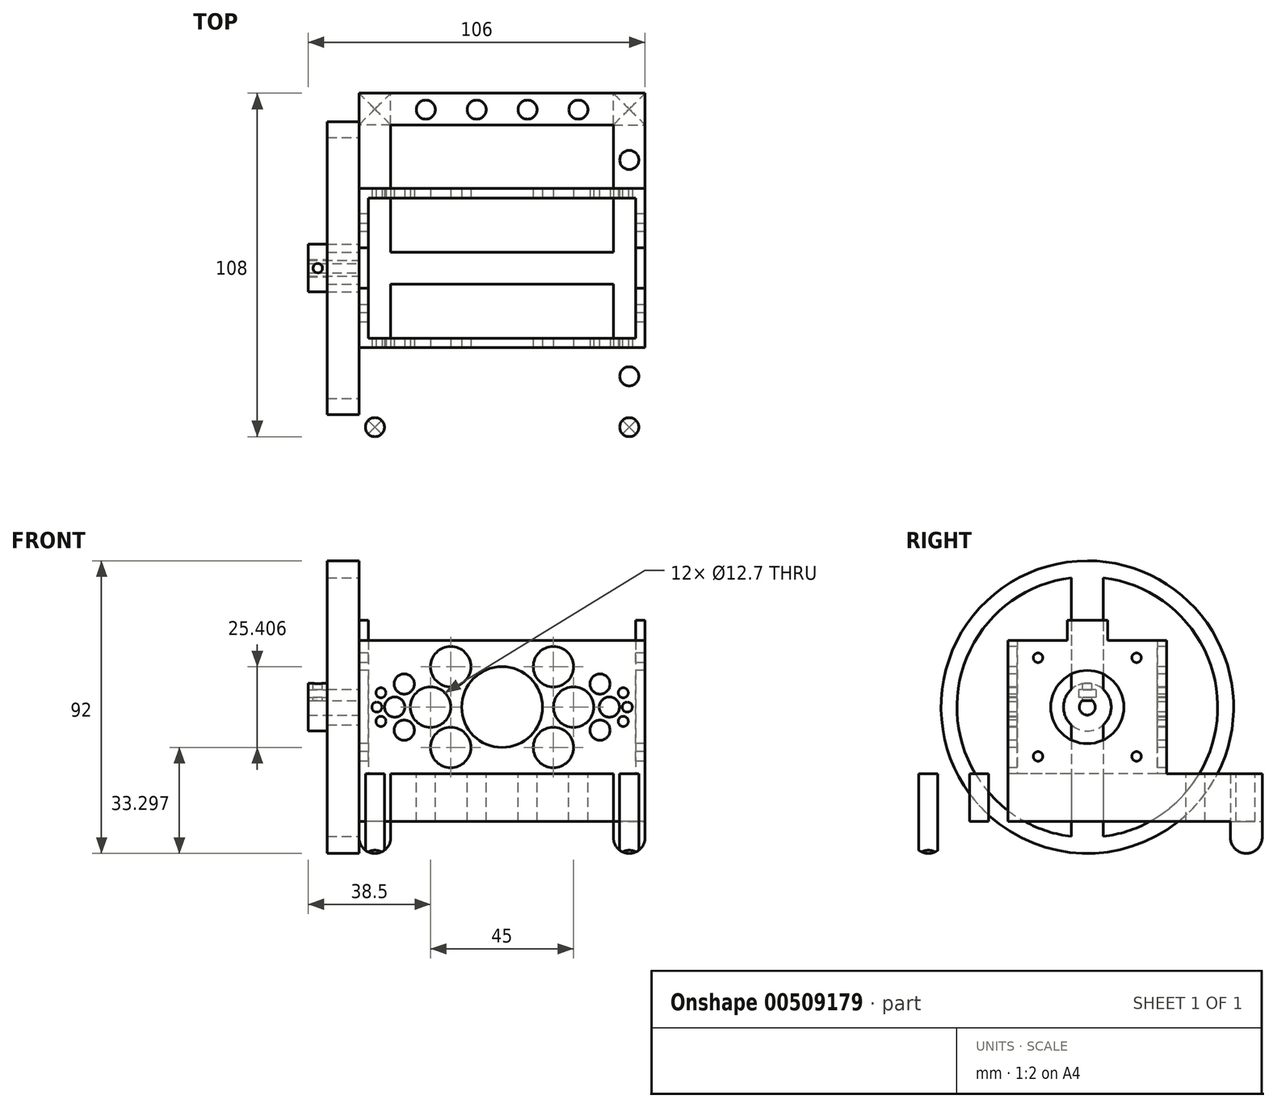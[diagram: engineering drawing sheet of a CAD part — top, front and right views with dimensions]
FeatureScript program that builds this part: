
annotation { "Feature Type Name" : "Feature", "Feature Type Description" : "" }
export const myFeature = defineFeature(function(context is Context, id is Id, definition is map)
    precondition{}
    {
        {
            var Q0;
            Q0=qCreatedBy(makeId("Top.planeOp"),FACE);
            var sketch = newSketch(context, id + "F0", { "sketchPlane" : qUnion([Q0])});
            skLineSegment(sketch, "E0.bottom", {"start": v(-45, 55) * mm, "end": v(45, 55) * mm});
            skLineSegment(sketch, "E0.top", {"start": v(-45, -55) * mm, "end": v(45, -55) * mm});
            skLineSegment(sketch, "E0.left", {"start": v(-45, 55) * mm, "end": v(-45, -55) * mm});
            skLineSegment(sketch, "E0.right", {"start": v(45, 55) * mm, "end": v(45, -55) * mm});
            skPoint(sketch, "E1", {"position": v(0, 55) * mm});
            skPoint(sketch, "E2", {"position": v(45, 0) * mm});
            skLineSegment(sketch, "E3.bottom", {"start": v(-35, 45) * mm, "end": v(35, 45) * mm});
            skLineSegment(sketch, "E3.top", {"start": v(-35, -45) * mm, "end": v(35, -45) * mm});
            skLineSegment(sketch, "E3.left", {"start": v(-35, 45) * mm, "end": v(-35, 5) * mm});
            skLineSegment(sketch, "E3.right", {"start": v(35, 45) * mm, "end": v(35, 5) * mm});
            skPoint(sketch, "E4", {"position": v(0, 45) * mm});
            skPoint(sketch, "E5", {"position": v(35, 0) * mm});
            skLineSegment(sketch, "E6", {"start": v(-35, 5) * mm, "end": v(35, 5) * mm});
            skLineSegment(sketch, "E7", {"start": v(-35, -5) * mm, "end": v(35, -5) * mm});
            skPoint(sketch, "E8", {"position": v(-35, 0) * mm});
            skLineSegment(sketch, "E9.trimOffspring", {"start": v(-35, -5) * mm, "end": v(-35, -45) * mm});
            skLineSegment(sketch, "E10.trimOffspring", {"start": v(35, -5) * mm, "end": v(35, -45) * mm});
            skSolve(sketch);
        }
        {
            var Q0;
            Q0 = qSketchRegion(id + "F0", true);
            extrude(context, id + "F1", {"entities" : qUnion([Q0]), "depth" : 15 * mm});
        }
        {
            var Q0;
            Q0=makeQuery(id+"F1.opExtrude","CAP_FACE",FACE,{"disambiguationData":[OSD([sQuery(id+"F0.wireOp",EDGE,"E0.bottom"),sQuery(id+"F0.wireOp",EDGE,"E0.top"),sQuery(id+"F0.wireOp",EDGE,"E0.left"),sQuery(id+"F0.wireOp",EDGE,"E0.right"),sQuery(id+"F0.wireOp",EDGE,"E3.bottom"),sQuery(id+"F0.wireOp",EDGE,"E3.top"),sQuery(id+"F0.wireOp",EDGE,"E3.left"),sQuery(id+"F0.wireOp",EDGE,"E3.right"),sQuery(id+"F0.wireOp",EDGE,"E6"),sQuery(id+"F0.wireOp",EDGE,"E7"),sQuery(id+"F0.wireOp",EDGE,"E9.trimOffspring"),sQuery(id+"F0.wireOp",EDGE,"E10.trimOffspring")])],"isStart":false});
            var sketch = newSketch(context, id + "F2", { "sketchPlane" : qUnion([Q0])});
            skLineSegment(sketch, "E11.bottom", {"start": v(45, 25) * mm, "end": v(42, 25) * mm});
            skLineSegment(sketch, "E11.top", {"start": v(45, -25) * mm, "end": v(42, -25) * mm});
            skLineSegment(sketch, "E11.left", {"start": v(45, 25) * mm, "end": v(45, -25) * mm});
            skLineSegment(sketch, "E11.right", {"start": v(42, 25) * mm, "end": v(42, -25) * mm});
            skPoint(sketch, "E12", {"position": v(45, 0) * mm});
            skLineSegment(sketch, "E13.bottom", {"start": v(45, 25) * mm, "end": v(35, 25) * mm});
            skLineSegment(sketch, "E13.top", {"start": v(45, 22) * mm, "end": v(35, 22) * mm});
            skLineSegment(sketch, "E13.left", {"start": v(45, 25) * mm, "end": v(45, 22) * mm});
            skLineSegment(sketch, "E13.right", {"start": v(35, 25) * mm, "end": v(35, 22) * mm});
            skLineSegment(sketch, "E14.MirrorCS", {"start": v(35, -25) * mm, "end": v(35, -22) * mm});
            skLineSegment(sketch, "E15.MirrorCS", {"start": v(45, -22) * mm, "end": v(35, -22) * mm});
            skLineSegment(sketch, "E16.MirrorCS", {"start": v(45, -25) * mm, "end": v(35, -25) * mm});
            skLineSegment(sketch, "E17.MirrorCS", {"start": v(-45, 25) * mm, "end": v(-45, 22) * mm});
            skLineSegment(sketch, "E18.MirrorCS", {"start": v(-35, 25) * mm, "end": v(-35, 22) * mm});
            skLineSegment(sketch, "E19.MirrorCS", {"start": v(-45, 25) * mm, "end": v(-42, 25) * mm});
            skLineSegment(sketch, "E20.MirrorCS", {"start": v(-45, -25) * mm, "end": v(-42, -25) * mm});
            skLineSegment(sketch, "E21.MirrorCS", {"start": v(-35, -25) * mm, "end": v(-35, -22) * mm});
            skLineSegment(sketch, "E22.MirrorCS", {"start": v(-42, 25) * mm, "end": v(-42, -25) * mm});
            skLineSegment(sketch, "E23.MirrorCS", {"start": v(-45, 25) * mm, "end": v(-35, 25) * mm});
            skLineSegment(sketch, "E24.MirrorCS", {"start": v(-45, -22) * mm, "end": v(-35, -22) * mm});
            skPoint(sketch, "E25.MirrorP", {"position": v(-45, 0) * mm});
            skLineSegment(sketch, "E26.MirrorCS", {"start": v(-45, -25) * mm, "end": v(-35, -25) * mm});
            skLineSegment(sketch, "E27.MirrorCS", {"start": v(-45, 25) * mm, "end": v(-45, -25) * mm});
            skLineSegment(sketch, "E28.MirrorCS", {"start": v(-45, 22) * mm, "end": v(-35, 22) * mm});
            skLineSegment(sketch, "E29", {"start": v(35, 25) * mm, "end": v(-35, 25) * mm});
            skLineSegment(sketch, "E30", {"start": v(-35, 22) * mm, "end": v(35, 22) * mm});
            skLineSegment(sketch, "E31", {"start": v(35, -22) * mm, "end": v(-35, -22) * mm});
            skLineSegment(sketch, "E32", {"start": v(-35, -25) * mm, "end": v(35, -25) * mm});
            skSolve(sketch);
        }
        {
            var Q0;
            Q0 = qSketchRegion(id + "F2", true);
            extrude(context, id + "F3", {"entities" : qUnion([Q0]), "operationType" : NewBodyOperationType.ADD, "depth" : 42 * mm});
        }
        {
            var Q0;
            Q0=makeQuery(id+"F1.opExtrude","CAP_FACE",FACE,{"disambiguationData":[OSD([sQuery(id+"F0.wireOp",EDGE,"E0.bottom"),sQuery(id+"F0.wireOp",EDGE,"E0.top"),sQuery(id+"F0.wireOp",EDGE,"E0.left"),sQuery(id+"F0.wireOp",EDGE,"E0.right"),sQuery(id+"F0.wireOp",EDGE,"E3.bottom"),sQuery(id+"F0.wireOp",EDGE,"E3.top"),sQuery(id+"F0.wireOp",EDGE,"E3.left"),sQuery(id+"F0.wireOp",EDGE,"E3.right"),sQuery(id+"F0.wireOp",EDGE,"E6"),sQuery(id+"F0.wireOp",EDGE,"E7"),sQuery(id+"F0.wireOp",EDGE,"E9.trimOffspring"),sQuery(id+"F0.wireOp",EDGE,"E10.trimOffspring")])],"isStart":true});
            var sketch = newSketch(context, id + "F4", { "sketchPlane" : qUnion([Q0])});
            skLineSegment(sketch, "E33.bottom", {"start": v(-35, -45) * mm, "end": v(-45, -45) * mm});
            skLineSegment(sketch, "E33.top", {"start": v(-35, -55) * mm, "end": v(-45, -55) * mm});
            skLineSegment(sketch, "E33.left", {"start": v(-35, -45) * mm, "end": v(-35, -55) * mm});
            skLineSegment(sketch, "E33.right", {"start": v(-45, -45) * mm, "end": v(-45, -55) * mm});
            skLineSegment(sketch, "E34.MirrorCS", {"start": v(-45, 45) * mm, "end": v(-45, 55) * mm});
            skLineSegment(sketch, "E35.MirrorCS", {"start": v(-35, 45) * mm, "end": v(-35, 55) * mm});
            skLineSegment(sketch, "E36.MirrorCS", {"start": v(-35, 55) * mm, "end": v(-45, 55) * mm});
            skLineSegment(sketch, "E37.MirrorCS", {"start": v(-35, 45) * mm, "end": v(-45, 45) * mm});
            skLineSegment(sketch, "E38.MirrorCS", {"start": v(35, 45) * mm, "end": v(45, 45) * mm});
            skLineSegment(sketch, "E39.MirrorCS", {"start": v(35, 55) * mm, "end": v(45, 55) * mm});
            skLineSegment(sketch, "E40.MirrorCS", {"start": v(35, 45) * mm, "end": v(35, 55) * mm});
            skLineSegment(sketch, "E41.MirrorCS", {"start": v(45, 45) * mm, "end": v(45, 55) * mm});
            skLineSegment(sketch, "E42.MirrorCS", {"start": v(45, -45) * mm, "end": v(45, -55) * mm});
            skLineSegment(sketch, "E43.MirrorCS", {"start": v(35, -45) * mm, "end": v(45, -45) * mm});
            skLineSegment(sketch, "E44.MirrorCS", {"start": v(35, -45) * mm, "end": v(35, -55) * mm});
            skLineSegment(sketch, "E45.MirrorCS", {"start": v(35, -55) * mm, "end": v(45, -55) * mm});
            skSolve(sketch);
        }
        {
            var Q0;
            Q0 = qSketchRegion(id + "F4", true);
            extrude(context, id + "F5", {"entities" : qUnion([Q0]), "operationType" : NewBodyOperationType.ADD, "depth" : 10 * mm});
        }
        {
            var Q0;
            Q0=makeQuery(id+"F5.boolean.opBoolean","MERGE",FACE,{"derivedFrom":[makeQuery(id+"F3.boolean.opBoolean","MERGE",FACE,{"derivedFrom":[makeQuery(id+"F1.opExtrude","SWEPT_FACE",FACE,{"disambiguationData":[OSD([sQuery(id+"F0.wireOp",EDGE,"E0.left")])]}),makeQuery(id+"F3.opExtrude","SWEPT_FACE",FACE,{"disambiguationData":[OSD([sQuery(id+"F2.wireOp",EDGE,"c03ca210-d2da-4281-a216-32e1d23c1b741.MirrorCS")])]}),makeQuery(id+"F3.opExtrude","SWEPT_FACE",FACE,{"disambiguationData":[OSD([sQuery(id+"F2.wireOp",EDGE,"2e68947a-544b-477c-b511-bde02374e1be1.MirrorCS")])]}),makeQuery(id+"F3.opExtrude","SWEPT_FACE",FACE,{"disambiguationData":[OSD([sQuery(id+"F2.wireOp",EDGE,"E27.MirrorCS")])]})]}),makeQuery(id+"F5.opExtrude","SWEPT_FACE",FACE,{"disambiguationData":[OSD([sQuery(id+"F4.wireOp",EDGE,"E33.right")])]}),makeQuery(id+"F5.opExtrude","SWEPT_FACE",FACE,{"disambiguationData":[OSD([sQuery(id+"F4.wireOp",EDGE,"E34.MirrorCS")])]})]});
            var sketch = newSketch(context, id + "F6", { "sketchPlane" : qUnion([Q0])});
            skLineSegment(sketch, "E46", {"start": v(-25, 15) * mm, "end": v(25, 15) * mm, "construction": true});
            skLineSegment(sketch, "E47", {"start": v(-25, 36) * mm, "end": v(25, 36) * mm, "construction": true});
            skCircle(sketch, "E48", {"center": v(0, 36) * mm, "radius": 11.5 * mm});
            skLineSegment(sketch, "E49", {"start": v(-15.5, 15) * mm, "end": v(-15.5, 57) * mm, "construction": true});
            skLineSegment(sketch, "E50.MirrorCS", {"start": v(15.5, 15) * mm, "end": v(15.5, 57) * mm, "construction": true});
            skLineSegment(sketch, "E51", {"start": v(-15.5, 51.5) * mm, "end": v(15.5, 51.5) * mm, "construction": true});
            skLineSegment(sketch, "E52.MirrorCS", {"start": v(-15.5, 20.5) * mm, "end": v(15.5, 20.5) * mm, "construction": true});
            skCircle(sketch, "E53", {"center": v(-15.5, 20.5) * mm, "radius": 1.5 * mm});
            skCircle(sketch, "E54.MirrorC", {"center": v(15.5, 20.5) * mm, "radius": 1.5 * mm});
            skCircle(sketch, "E55.MirrorC", {"center": v(15.5, 51.5) * mm, "radius": 1.5 * mm});
            skCircle(sketch, "E56.MirrorC", {"center": v(-15.5, 51.5) * mm, "radius": 1.5 * mm});
            skSolve(sketch);
        }
        {
            var Q0;
            Q0 = qSketchRegion(id + "F6", true);
            var Q1;
            Q1=makeQuery(id+"F5.boolean.opBoolean","MERGE",FACE,{"derivedFrom":[makeQuery(id+"F3.boolean.opBoolean","MERGE",FACE,{"derivedFrom":[makeQuery(id+"F1.opExtrude","SWEPT_FACE",FACE,{"disambiguationData":[OSD([sQuery(id+"F0.wireOp",EDGE,"E0.right")])]}),makeQuery(id+"F3.opExtrude","SWEPT_FACE",FACE,{"disambiguationData":[OSD([sQuery(id+"F2.wireOp",EDGE,"VcPYBWTV-BgIg-0Cdf-vaFz-7VsyfP8OD9oq.left")])]}),makeQuery(id+"F3.opExtrude","SWEPT_FACE",FACE,{"disambiguationData":[OSD([sQuery(id+"F2.wireOp",EDGE,"2e68947a-544b-477c-b511-bde02374e1be4.MirrorCS")])]}),makeQuery(id+"F3.opExtrude","SWEPT_FACE",FACE,{"disambiguationData":[OSD([sQuery(id+"F2.wireOp",EDGE,"E11.left"),sQuery(id+"F2.wireOp",EDGE,"E13.left")])]})]}),makeQuery(id+"F5.opExtrude","SWEPT_FACE",FACE,{"disambiguationData":[OSD([sQuery(id+"F4.wireOp",EDGE,"E41.MirrorCS")])]}),makeQuery(id+"F5.opExtrude","SWEPT_FACE",FACE,{"disambiguationData":[OSD([sQuery(id+"F4.wireOp",EDGE,"E42.MirrorCS")])]})]});
            extrude(context, id + "F7", {"entities" : qUnion([Q0]), "operationType" : NewBodyOperationType.REMOVE, "endBound" : BoundingType.UP_TO_SURFACE, "oppositeDirection" : true, "endBoundEntityFace" : qUnion([Q1]), "depth" : 25.4 * mm});
        }
        {
            var Q0;
            Q0=makeQuery(id+"F5.opExtrude","CAP_FACE",FACE,{"disambiguationData":[OSD([sQuery(id+"F4.wireOp",EDGE,"E38.MirrorCS"),sQuery(id+"F4.wireOp",EDGE,"E39.MirrorCS"),sQuery(id+"F4.wireOp",EDGE,"E40.MirrorCS"),sQuery(id+"F4.wireOp",EDGE,"E41.MirrorCS")])],"isStart":false});
            var Q1;
            Q1=makeQuery(id+"F5.opExtrude","CAP_FACE",FACE,{"disambiguationData":[OSD([sQuery(id+"F4.wireOp",EDGE,"E34.MirrorCS"),sQuery(id+"F4.wireOp",EDGE,"E35.MirrorCS"),sQuery(id+"F4.wireOp",EDGE,"E36.MirrorCS"),sQuery(id+"F4.wireOp",EDGE,"E37.MirrorCS")])],"isStart":false});
            var Q2;
            Q2=makeQuery(id+"F5.opExtrude","CAP_EDGE",EDGE,{"disambiguationData":[OSD([sQuery(id+"F4.wireOp",EDGE,"E42.MirrorCS")])],"isStart":false});
            var Q3;
            Q3=makeQuery(id+"F5.opExtrude","CAP_FACE",FACE,{"disambiguationData":[OSD([sQuery(id+"F4.wireOp",EDGE,"E42.MirrorCS"),sQuery(id+"F4.wireOp",EDGE,"E43.MirrorCS"),sQuery(id+"F4.wireOp",EDGE,"E44.MirrorCS"),sQuery(id+"F4.wireOp",EDGE,"E45.MirrorCS")])],"isStart":false});
            var Q4;
            Q4=makeQuery(id+"F5.opExtrude","CAP_FACE",FACE,{"disambiguationData":[OSD([sQuery(id+"F4.wireOp",EDGE,"E33.bottom"),sQuery(id+"F4.wireOp",EDGE,"E33.top"),sQuery(id+"F4.wireOp",EDGE,"E33.left"),sQuery(id+"F4.wireOp",EDGE,"E33.right")])],"isStart":false});
            fillet(context, id + "F8", {"entities" : qUnion([Q0, Q1, Q2, Q3, Q4]), "radius" : 5 * mm, "tangentPropagation" : true, "allowEdgeOverflow" : false});
        }
        {
            var Q0;
            Q0=makeQuery(id+"F3.opExtrude","SWEPT_FACE",FACE,{"disambiguationData":[OSD([sQuery(id+"F2.wireOp",EDGE,"E16.MirrorCS"),sQuery(id+"F2.wireOp",EDGE,"E26.MirrorCS"),sQuery(id+"F2.wireOp",EDGE,"E32")])]});
            var sketch = newSketch(context, id + "F9", { "sketchPlane" : qUnion([Q0])});
            skLineSegment(sketch, "E57", {"start": v(-45, 36) * mm, "end": v(45, 36) * mm, "construction": true});
            skCircle(sketch, "E58", {"center": v(0, 36) * mm, "radius": 12.7 * mm});
            skCircle(sketch, "E59", {"center": v(22.5, 36) * mm, "radius": 6.35 * mm});
            skLineSegment(sketch, "E60", {"start": v(0, 36) * mm, "end": v(45, 36) * mm, "construction": true});
            skCircle(sketch, "E61.MirrorC", {"center": v(-22.5, 36) * mm, "radius": 6.35 * mm});
            skLineSegment(sketch, "E62", {"start": v(22.5, 36) * mm, "end": v(45, 36) * mm, "construction": true});
            skPoint(sketch, "E63", {"position": v(33.75, 36) * mm});
            skCircle(sketch, "E64", {"center": v(33.75, 36) * mm, "radius": 3.18 * mm});
            skCircle(sketch, "E65.MirrorC", {"center": v(-33.75, 36) * mm, "radius": 3.18 * mm});
            skCircle(sketch, "E66", {"center": v(16.15, 23.3) * mm, "radius": 6.35 * mm});
            skCircle(sketch, "E67.MirrorC", {"center": v(16.15, 48.7) * mm, "radius": 6.35 * mm});
            skCircle(sketch, "E68.MirrorC", {"center": v(-16.15, 48.7) * mm, "radius": 6.35 * mm});
            skCircle(sketch, "E69.MirrorC", {"center": v(-16.15, 23.3) * mm, "radius": 6.35 * mm});
            skCircle(sketch, "E70", {"center": v(30.79, 28.73) * mm, "radius": 3.18 * mm});
            skCircle(sketch, "E71.MirrorC", {"center": v(30.79, 43.27) * mm, "radius": 3.18 * mm});
            skCircle(sketch, "E72.MirrorC", {"center": v(-30.79, 43.27) * mm, "radius": 3.18 * mm});
            skCircle(sketch, "E73.MirrorC", {"center": v(-30.79, 28.73) * mm, "radius": 3.18 * mm});
            skCircle(sketch, "E74", {"center": v(39.38, 36) * mm, "radius": 1.59 * mm});
            skLineSegment(sketch, "E75", {"start": v(33.75, 36) * mm, "end": v(45, 36) * mm, "construction": true});
            skPoint(sketch, "E76", {"position": v(39.37, 36) * mm});
            skCircle(sketch, "E77", {"center": v(38.1, 31.5) * mm, "radius": 1.59 * mm});
            skCircle(sketch, "E78.MirrorC", {"center": v(38.1, 40.5) * mm, "radius": 1.59 * mm});
            skCircle(sketch, "E79.MirrorC", {"center": v(-38.1, 40.5) * mm, "radius": 1.59 * mm});
            skCircle(sketch, "E80.MirrorC", {"center": v(-38.1, 31.5) * mm, "radius": 1.59 * mm});
            skCircle(sketch, "E81.MirrorC", {"center": v(-39.38, 36) * mm, "radius": 1.59 * mm});
            skSolve(sketch);
        }
        {
            var Q0;
            Q0 = qSketchRegion(id + "F9", true);
            extrude(context, id + "F10", {"entities" : qUnion([Q0]), "operationType" : NewBodyOperationType.REMOVE, "endBound" : BoundingType.THROUGH_ALL, "oppositeDirection" : true, "depth" : 25.4 * mm});
        }
        {
            var Q0;
            Q0=makeQuery(id+"F3.opExtrude","CAP_FACE",FACE,{"disambiguationData":[OSD([sQuery(id+"F2.wireOp",EDGE,"E11.left"),sQuery(id+"F2.wireOp",EDGE,"E11.right"),sQuery(id+"F2.wireOp",EDGE,"E13.bottom"),sQuery(id+"F2.wireOp",EDGE,"E13.top"),sQuery(id+"F2.wireOp",EDGE,"E13.left"),sQuery(id+"F2.wireOp",EDGE,"E15.MirrorCS"),sQuery(id+"F2.wireOp",EDGE,"E16.MirrorCS"),sQuery(id+"F2.wireOp",EDGE,"E22.MirrorCS"),sQuery(id+"F2.wireOp",EDGE,"E23.MirrorCS"),sQuery(id+"F2.wireOp",EDGE,"E24.MirrorCS"),sQuery(id+"F2.wireOp",EDGE,"E26.MirrorCS"),sQuery(id+"F2.wireOp",EDGE,"E27.MirrorCS"),sQuery(id+"F2.wireOp",EDGE,"E28.MirrorCS"),sQuery(id+"F2.wireOp",EDGE,"E29"),sQuery(id+"F2.wireOp",EDGE,"E30"),sQuery(id+"F2.wireOp",EDGE,"E31"),sQuery(id+"F2.wireOp",EDGE,"E32")])],"isStart":false});
            var sketch = newSketch(context, id + "F11", { "sketchPlane" : qUnion([Q0])});
            skLineSegment(sketch, "E82.bottom", {"start": v(45, -6.35) * mm, "end": v(42, -6.35) * mm});
            skLineSegment(sketch, "E82.top", {"start": v(45, 6.35) * mm, "end": v(42, 6.35) * mm});
            skLineSegment(sketch, "E82.left", {"start": v(45, -6.35) * mm, "end": v(45, 6.35) * mm});
            skLineSegment(sketch, "E82.right", {"start": v(42, -6.35) * mm, "end": v(42, 6.35) * mm});
            skPoint(sketch, "E83", {"position": v(45, 0) * mm});
            skLineSegment(sketch, "E84.MirrorCS", {"start": v(-45, -6.35) * mm, "end": v(-42, -6.35) * mm});
            skLineSegment(sketch, "E85.MirrorCS", {"start": v(-45, 6.35) * mm, "end": v(-42, 6.35) * mm});
            skLineSegment(sketch, "E86.MirrorCS", {"start": v(-42, -6.35) * mm, "end": v(-42, 6.35) * mm});
            skLineSegment(sketch, "E87.MirrorCS", {"start": v(-45, -6.35) * mm, "end": v(-45, 6.35) * mm});
            skPoint(sketch, "E88.MirrorP", {"position": v(-45, 0) * mm});
            skSolve(sketch);
        }
        {
            var Q0;
            Q0 = qSketchRegion(id + "F11", true);
            extrude(context, id + "F12", {"entities" : qUnion([Q0]), "operationType" : NewBodyOperationType.ADD, "depth" : 6.35 * mm});
        }
        {
            var Q0;
            Q0=makeQuery(id+"F12.boolean.opBoolean","MERGE",FACE,{"derivedFrom":[makeQuery(id+"F5.boolean.opBoolean","MERGE",FACE,{"derivedFrom":[makeQuery(id+"F3.boolean.opBoolean","MERGE",FACE,{"derivedFrom":[makeQuery(id+"F1.opExtrude","SWEPT_FACE",FACE,{"disambiguationData":[OSD([sQuery(id+"F0.wireOp",EDGE,"E0.left")])]}),makeQuery(id+"F3.opExtrude","SWEPT_FACE",FACE,{"disambiguationData":[OSD([sQuery(id+"F2.wireOp",EDGE,"E27.MirrorCS")])]})]}),makeQuery(id+"F5.opExtrude","SWEPT_FACE",FACE,{"disambiguationData":[OSD([sQuery(id+"F4.wireOp",EDGE,"E33.right")])]}),makeQuery(id+"F5.opExtrude","SWEPT_FACE",FACE,{"disambiguationData":[OSD([sQuery(id+"F4.wireOp",EDGE,"E34.MirrorCS")])]})]}),makeQuery(id+"F12.opExtrude","SWEPT_FACE",FACE,{"disambiguationData":[OSD([sQuery(id+"F11.wireOp",EDGE,"E87.MirrorCS")])]})]});
            var sketch = newSketch(context, id + "F13", { "sketchPlane" : qUnion([Q0])});
            skCircle(sketch, "E89", {"center": v(0, 36) * mm, "radius": 46 * mm});
            skLineSegment(sketch, "E90", {"start": v(-50, -5) * mm, "end": v(-50, -10) * mm, "construction": true});
            skLineSegment(sketch, "E91", {"start": v(-50, -10) * mm, "end": v(30.9, -10) * mm, "construction": true});
            skArc(sketch, "E92", {"start": v(-5, 76.7) * mm, "mid": v(-41, 36) * mm, "end": v(-5, -4.7) * mm});
            skLineSegment(sketch, "E93", {"start": v(-5, 76.7) * mm, "end": v(-5, 41.6) * mm});
            skLineSegment(sketch, "E94", {"start": v(5, 76.7) * mm, "end": v(5, 41.6) * mm});
            skLineSegment(sketch, "E95", {"start": v(-5, 70.26) * mm, "end": v(5, 70.26) * mm, "construction": true});
            skPoint(sketch, "E96", {"position": v(0, 70.26) * mm});
            skArc(sketch, "E97.trimOffspring", {"start": v(5, -4.7) * mm, "mid": v(41, 36) * mm, "end": v(5, 76.7) * mm});
            skArc(sketch, "E98", {"start": v(-5, 41.6) * mm, "mid": v(-7.5, 36) * mm, "end": v(-5, 30.4) * mm});
            skLineSegment(sketch, "E99.trimOffspring", {"start": v(-5, 30.4) * mm, "end": v(-5, -4.7) * mm});
            skLineSegment(sketch, "E100.trimOffspring", {"start": v(5, 30.4) * mm, "end": v(5, -4.7) * mm});
            skArc(sketch, "E101", {"start": v(-1.5, 38) * mm, "mid": v(0, 33.5) * mm, "end": v(1.5, 38) * mm});
            skLineSegment(sketch, "E102", {"start": v(-1.5, 38) * mm, "end": v(1.5, 38) * mm});
            skArc(sketch, "E103.trimOffspring", {"start": v(5, 30.4) * mm, "mid": v(7.5, 36) * mm, "end": v(5, 41.6) * mm});
            skSolve(sketch);
        }
        {
            var Q0;
            Q0 = qSketchRegion(id + "F13", true);
            extrude(context, id + "F14", {"entities" : qUnion([Q0]), "depth" : 10 * mm});
        }
        {
            var Q0;
            Q0=makeQuery(id+"F14.opExtrude","CAP_FACE",FACE,{"disambiguationData":[OSD([sQuery(id+"F13.wireOp",EDGE,"E89"),sQuery(id+"F13.wireOp",EDGE,"E92"),sQuery(id+"F13.wireOp",EDGE,"E93"),sQuery(id+"F13.wireOp",EDGE,"E94"),sQuery(id+"F13.wireOp",EDGE,"E97.trimOffspring"),sQuery(id+"F13.wireOp",EDGE,"E98"),sQuery(id+"F13.wireOp",EDGE,"E99.trimOffspring"),sQuery(id+"F13.wireOp",EDGE,"E100.trimOffspring"),sQuery(id+"F13.wireOp",EDGE,"E101"),sQuery(id+"F13.wireOp",EDGE,"E102"),sQuery(id+"F13.wireOp",EDGE,"E103.trimOffspring")])],"isStart":false});
            var sketch = newSketch(context, id + "F15", { "sketchPlane" : qUnion([Q0])});
            skCircle(sketch, "E104", {"center": v(0, 36) * mm, "radius": 7.5 * mm});
            skLineSegment(sketch, "E105.bottom", {"start": v(-2.75, 41.4) * mm, "end": v(2.75, 41.4) * mm});
            skLineSegment(sketch, "E105.top", {"start": v(-2.75, 39) * mm, "end": v(2.75, 39) * mm});
            skLineSegment(sketch, "E105.left", {"start": v(-2.75, 41.4) * mm, "end": v(-2.75, 39) * mm});
            skLineSegment(sketch, "E105.right", {"start": v(2.75, 41.4) * mm, "end": v(2.75, 39) * mm});
            skPoint(sketch, "E106", {"position": v(0, 41.4) * mm});
            skArc(sketch, "E107", {"start": v(-1.5, 38) * mm, "mid": v(0, 33.5) * mm, "end": v(1.5, 38) * mm});
            skLineSegment(sketch, "E108", {"start": v(-1.5, 38) * mm, "end": v(1.5, 38) * mm});
            skSolve(sketch);
        }
        {
            var Q0;
            Q0 = qSketchRegion(id + "F15", true);
            extrude(context, id + "F16", {"entities" : qUnion([Q0]), "operationType" : NewBodyOperationType.ADD, "depth" : 6 * mm, "offsetDistance" : 25.4 * mm});
        }
        {
            var Q0;
            Q0=qCreatedBy(makeId("Top.planeOp"),FACE);
            cPlane(context, id + "F17", {"entities" : qUnion([Q0]), "cplaneType" : CPlaneType.OFFSET, "offset" : 50.8 * mm, "width" : 152.4 * mm, "height" : 152.4 * mm});
        }
        {
            var Q0;
            Q0=qCreatedBy(id+"F17.planeOp",FACE);
            var sketch = newSketch(context, id + "F18", { "sketchPlane" : qUnion([Q0])});
            skCircle(sketch, "E109", {"center": v(-58, 0) * mm, "radius": 1.5 * mm});
            skLineSegment(sketch, "E110", {"start": v(-61, 0) * mm, "end": v(-55, 0) * mm, "construction": true});
            skSolve(sketch);
        }
        {
            var Q0;
            Q0=makeQuery(id+"F18.imprint","IMPRINT",FACE,{"disambiguationData":[TD([[makeQuery(id+"F18.imprint","IMPRINT",EDGE,{"derivedFrom":sQuery(id+"F18.wireOp",EDGE,"E109")}),1.0]])]});
            var Q1;
            Q1=makeQuery(id+"F16.boolean.opBoolean","MERGE",FACE,{"derivedFrom":[makeQuery(id+"F14.opExtrude","SWEPT_FACE",FACE,{"disambiguationData":[OSD([sQuery(id+"F13.wireOp",EDGE,"E102")])]}),makeQuery(id+"F16.opExtrude","SWEPT_FACE",FACE,{"disambiguationData":[OSD([sQuery(id+"F15.wireOp",EDGE,"E108")])]})]});
            extrude(context, id + "F19", {"entities" : qUnion([Q0]), "operationType" : NewBodyOperationType.REMOVE, "endBound" : BoundingType.UP_TO_SURFACE, "oppositeDirection" : true, "endBoundEntityFace" : qUnion([Q1]), "depth" : 25.4 * mm});
        }
        {
            var Q0;
            Q0=makeQuery(id+"F16.opExtrude","CAP_FACE",FACE,{"disambiguationData":[OSD([sQuery(id+"F15.wireOp",EDGE,"E104"),sQuery(id+"F15.wireOp",EDGE,"E105.bottom"),sQuery(id+"F15.wireOp",EDGE,"E105.top"),sQuery(id+"F15.wireOp",EDGE,"E105.left"),sQuery(id+"F15.wireOp",EDGE,"E105.right"),sQuery(id+"F15.wireOp",EDGE,"E107"),sQuery(id+"F15.wireOp",EDGE,"E108")])],"isStart":false});
            var sketch = newSketch(context, id + "F20", { "sketchPlane" : qUnion([Q0])});
            skLineSegment(sketch, "E111.bottom", {"start": v(-2.75, 41.4) * mm, "end": v(2.75, 41.4) * mm});
            skLineSegment(sketch, "E111.top", {"start": v(-2.75, 39) * mm, "end": v(2.75, 39) * mm});
            skLineSegment(sketch, "E111.left", {"start": v(-2.75, 41.4) * mm, "end": v(-2.75, 39) * mm});
            skLineSegment(sketch, "E111.right", {"start": v(2.75, 41.4) * mm, "end": v(2.75, 39) * mm});
            skSolve(sketch);
        }
        {
            var Q0;
            Q0=makeQuery(id+"F20.imprint","IMPRINT",FACE,{"disambiguationData":[TD([[makeQuery(id+"F20.imprint","IMPRINT",EDGE,{"derivedFrom":sQuery(id+"F20.wireOp",EDGE,"E111.bottom")}),-1.0]])]});
            extrude(context, id + "F21", {"entities" : qUnion([Q0]), "operationType" : NewBodyOperationType.REMOVE, "oppositeDirection" : true, "depth" : 2.5 * mm});
        }
        {
            var Q0;
            {var subQ0=sQuery(id+"F0.wireOp",EDGE,"E3.top");var subQ1=sQuery(id+"F0.wireOp",EDGE,"E0.right");var subQ2=sQuery(id+"F0.wireOp",EDGE,"E0.left");var subQ3=sQuery(id+"F0.wireOp",EDGE,"E0.top");var subQ6=sQuery(id+"F0.wireOp",EDGE,"E9.trimOffspring");var subQ11=sQuery(id+"F0.wireOp",EDGE,"E10.trimOffspring");Q0=makeQuery(id+"F3.boolean.opBoolean","SPLIT",FACE,{"disambiguationData":[TD([makeQuery(id+"F1.opExtrude","SWEPT_FACE",FACE,{"disambiguationData":[OSD([subQ3])]})])],"derivedFrom":makeQuery(id+"F1.opExtrude","CAP_FACE",FACE,{"disambiguationData":[OSD([sQuery(id+"F0.wireOp",EDGE,"E0.bottom"),subQ3,subQ2,subQ1,sQuery(id+"F0.wireOp",EDGE,"E3.bottom"),subQ0,sQuery(id+"F0.wireOp",EDGE,"E3.left"),sQuery(id+"F0.wireOp",EDGE,"E3.right"),sQuery(id+"F0.wireOp",EDGE,"E6"),sQuery(id+"F0.wireOp",EDGE,"E7"),subQ6,subQ11])],"isStart":false})});}
            var sketch = newSketch(context, id + "F22", { "sketchPlane" : qUnion([Q0])});
            skLineSegment(sketch, "E112", {"start": v(-45, -50) * mm, "end": v(45, -50) * mm, "construction": true});
            skLineSegment(sketch, "E113", {"start": v(14.93, -45) * mm, "end": v(14.93, -55) * mm, "construction": true});
            skPoint(sketch, "E114", {"position": v(14.93, -50) * mm});
            skCircle(sketch, "E115", {"center": v(-40, -50) * mm, "radius": 3 * mm});
            skLineSegment(sketch, "E116", {"start": v(-45, -36.45) * mm, "end": v(-35, -36.45) * mm, "construction": true});
            skPoint(sketch, "E117", {"position": v(-40, -36.45) * mm});
            skLineSegment(sketch, "E118", {"start": v(-40, -36.45) * mm, "end": v(-40, -55) * mm, "construction": true});
            skCircle(sketch, "E119.0.1.0", {"center": v(-40, 49.82) * mm, "radius": 3 * mm});
            skCircle(sketch, "E119.1.0.0", {"center": v(-24, -50) * mm, "radius": 3 * mm});
            skCircle(sketch, "E119.1.1.0", {"center": v(-24, 49.82) * mm, "radius": 3 * mm});
            skCircle(sketch, "E119.2.0.0", {"center": v(-8, -50) * mm, "radius": 3 * mm});
            skCircle(sketch, "E119.2.1.0", {"center": v(-8, 49.82) * mm, "radius": 3 * mm});
            skCircle(sketch, "E119.3.0.0", {"center": v(8, -50) * mm, "radius": 3 * mm});
            skCircle(sketch, "E119.3.1.0", {"center": v(8, 49.82) * mm, "radius": 3 * mm});
            skCircle(sketch, "E119.4.0.0", {"center": v(24, -50) * mm, "radius": 3 * mm});
            skCircle(sketch, "E119.4.1.0", {"center": v(24, 49.82) * mm, "radius": 3 * mm});
            skCircle(sketch, "E119.5.0.0", {"center": v(40, -50) * mm, "radius": 3 * mm});
            skCircle(sketch, "E119.5.1.0", {"center": v(40, 49.82) * mm, "radius": 3 * mm});
            skLineSegment(sketch, "E119.direction1", {"start": v(-40, -50) * mm, "end": v(-24, -50) * mm, "construction": true});
            skLineSegment(sketch, "E119.direction2", {"start": v(-40, -50) * mm, "end": v(-40, 49.82) * mm, "construction": true});
            skLineSegment(sketch, "E120", {"start": v(0, 0) * mm, "end": v(0, -50) * mm, "construction": true});
            skPoint(sketch, "E121", {"position": v(0, -25) * mm});
            skCircle(sketch, "E122.MirrorC", {"center": v(-24, 0) * mm, "radius": 3 * mm});
            skCircle(sketch, "E123.MirrorC", {"center": v(-8, 0) * mm, "radius": 3 * mm});
            skCircle(sketch, "E124.MirrorC", {"center": v(8, 0) * mm, "radius": 3 * mm});
            skCircle(sketch, "E125.MirrorC", {"center": v(24, 0) * mm, "radius": 3 * mm});
            skLineSegment(sketch, "E126", {"start": v(45, -55) * mm, "end": v(35, -45) * mm, "construction": true});
            skCircle(sketch, "E127.MirrorC", {"center": v(40, -34) * mm, "radius": 3 * mm});
            skCircle(sketch, "E128.MirrorC", {"center": v(40, 34) * mm, "radius": 3 * mm});
            skCircle(sketch, "E129.MirrorC", {"center": v(-40, 34) * mm, "radius": 3 * mm});
            skCircle(sketch, "E130.MirrorC", {"center": v(-40, -34) * mm, "radius": 3 * mm});
            skSolve(sketch);
        }
        {
            var Q0;
            Q0=makeQuery(id+"F22.imprint","IMPRINT",FACE,{"disambiguationData":[TD([[makeQuery(id+"F22.imprint","IMPRINT",EDGE,{"derivedFrom":sQuery(id+"F22.wireOp",EDGE,"E119.1.0.0")}),1.0]])]});
            var Q1;
            Q1=makeQuery(id+"F22.imprint","IMPRINT",FACE,{"disambiguationData":[TD([[makeQuery(id+"F22.imprint","IMPRINT",EDGE,{"derivedFrom":sQuery(id+"F22.wireOp",EDGE,"E119.2.0.0")}),1.0]])]});
            var Q2;
            Q2=makeQuery(id+"F22.imprint","IMPRINT",FACE,{"disambiguationData":[TD([[makeQuery(id+"F22.imprint","IMPRINT",EDGE,{"derivedFrom":sQuery(id+"F22.wireOp",EDGE,"E119.3.0.0")}),1.0]])]});
            var Q3;
            Q3=makeQuery(id+"F22.imprint","IMPRINT",FACE,{"disambiguationData":[TD([[makeQuery(id+"F22.imprint","IMPRINT",EDGE,{"derivedFrom":sQuery(id+"F22.wireOp",EDGE,"E119.4.0.0")}),1.0]])]});
            var Q4;
            Q4=makeQuery(id+"F22.imprint","IMPRINT",FACE,{"disambiguationData":[TD([[makeQuery(id+"F22.imprint","IMPRINT",EDGE,{"derivedFrom":sQuery(id+"F22.wireOp",EDGE,"E119.4.1.0")}),1.0]])]});
            var Q5;
            Q5=makeQuery(id+"F22.imprint","IMPRINT",FACE,{"disambiguationData":[TD([[makeQuery(id+"F22.imprint","IMPRINT",EDGE,{"derivedFrom":sQuery(id+"F22.wireOp",EDGE,"E119.3.1.0")}),1.0]])]});
            var Q6;
            Q6=makeQuery(id+"F22.imprint","IMPRINT",FACE,{"disambiguationData":[TD([[makeQuery(id+"F22.imprint","IMPRINT",EDGE,{"derivedFrom":sQuery(id+"F22.wireOp",EDGE,"E119.2.1.0")}),1.0]])]});
            var Q7;
            Q7=makeQuery(id+"F22.imprint","IMPRINT",FACE,{"disambiguationData":[TD([[makeQuery(id+"F22.imprint","IMPRINT",EDGE,{"derivedFrom":sQuery(id+"F22.wireOp",EDGE,"E119.1.1.0")}),1.0]])]});
            var Q8;
            Q8=makeQuery(id+"F22.imprint","IMPRINT",FACE,{"disambiguationData":[TD([[makeQuery(id+"F22.imprint","IMPRINT",EDGE,{"derivedFrom":sQuery(id+"F22.wireOp",EDGE,"E123.MirrorC")}),-1.0]])]});
            var Q9;
            Q9=makeQuery(id+"F22.imprint","IMPRINT",FACE,{"disambiguationData":[TD([[makeQuery(id+"F22.imprint","IMPRINT",EDGE,{"derivedFrom":sQuery(id+"F22.wireOp",EDGE,"E122.MirrorC")}),-1.0]])]});
            var Q10;
            Q10=makeQuery(id+"F22.imprint","IMPRINT",FACE,{"disambiguationData":[TD([[makeQuery(id+"F22.imprint","IMPRINT",EDGE,{"derivedFrom":sQuery(id+"F22.wireOp",EDGE,"E124.MirrorC")}),-1.0]])]});
            var Q11;
            Q11=makeQuery(id+"F22.imprint","IMPRINT",FACE,{"disambiguationData":[TD([[makeQuery(id+"F22.imprint","IMPRINT",EDGE,{"derivedFrom":sQuery(id+"F22.wireOp",EDGE,"E125.MirrorC")}),-1.0]])]});
            var Q12;
            Q12=makeQuery(id+"F22.imprint","IMPRINT",FACE,{"disambiguationData":[TD([[makeQuery(id+"F22.imprint","IMPRINT",EDGE,{"derivedFrom":sQuery(id+"F22.wireOp",EDGE,"E127.MirrorC")}),-1.0]])]});
            var Q13;
            Q13=makeQuery(id+"F22.imprint","IMPRINT",FACE,{"disambiguationData":[TD([[makeQuery(id+"F22.imprint","IMPRINT",EDGE,{"derivedFrom":sQuery(id+"F22.wireOp",EDGE,"E128.MirrorC")}),1.0]])]});
            var Q14;
            Q14=makeQuery(id+"F22.imprint","IMPRINT",FACE,{"disambiguationData":[TD([[makeQuery(id+"F22.imprint","IMPRINT",EDGE,{"derivedFrom":sQuery(id+"F22.wireOp",EDGE,"E129.MirrorC")}),-1.0]])]});
            var Q15;
            Q15=makeQuery(id+"F22.imprint","IMPRINT",FACE,{"disambiguationData":[TD([[makeQuery(id+"F22.imprint","IMPRINT",EDGE,{"derivedFrom":sQuery(id+"F22.wireOp",EDGE,"E130.MirrorC")}),1.0]])]});
            extrude(context, id + "F23", {"entities" : qUnion([Q0, Q1, Q2, Q3, Q4, Q5, Q6, Q7, Q8, Q9, Q10, Q11, Q12, Q13, Q14, Q15]), "operationType" : NewBodyOperationType.REMOVE, "oppositeDirection" : true, "depth" : 25.4 * mm});
        }
    });
